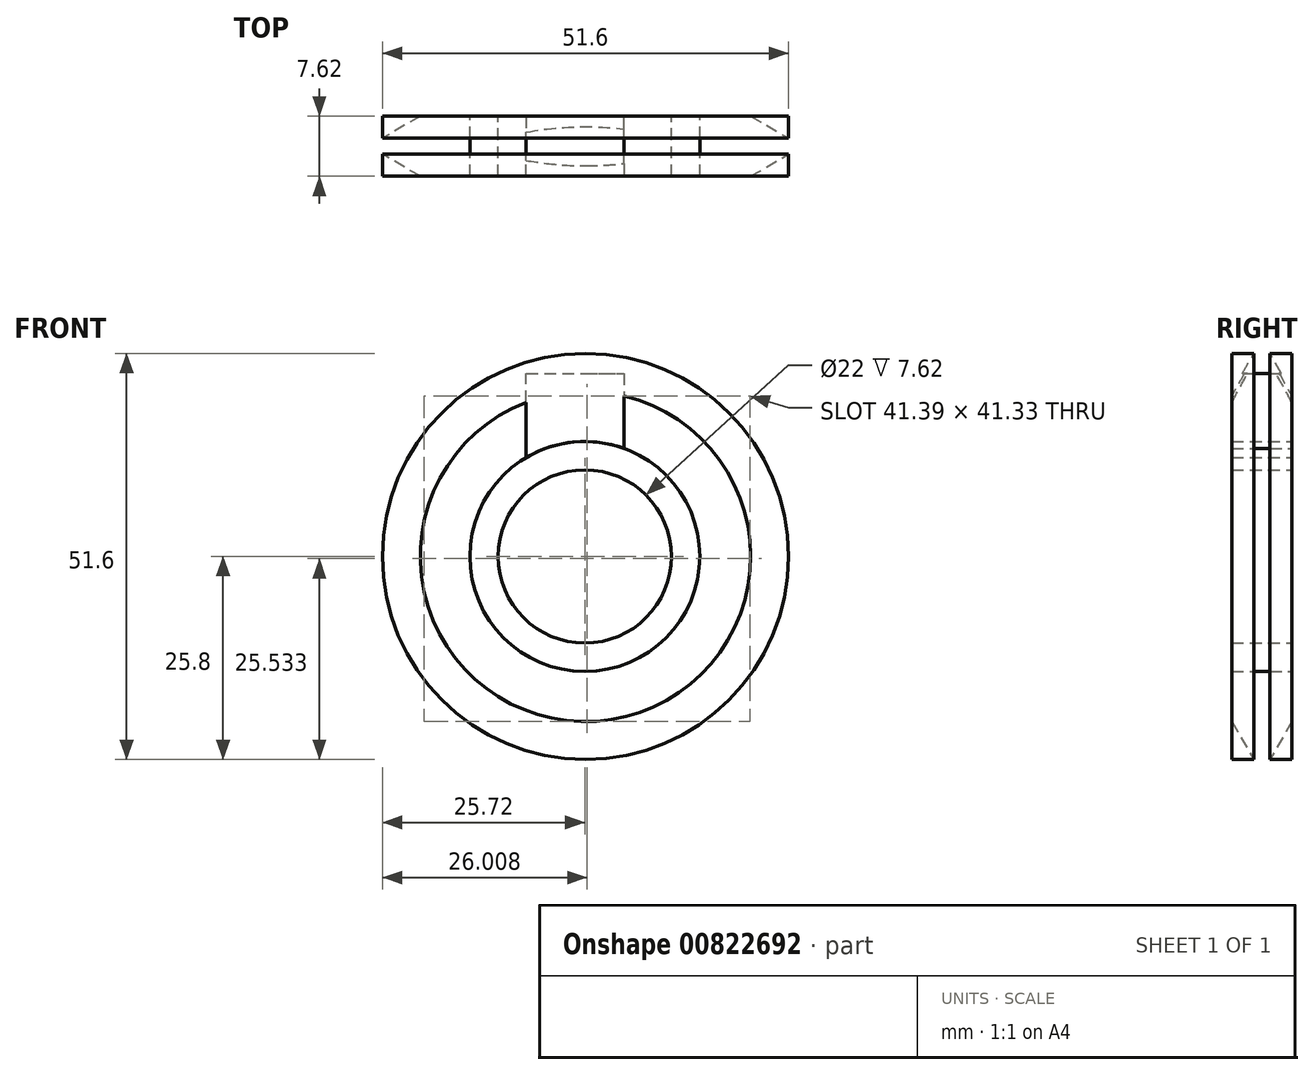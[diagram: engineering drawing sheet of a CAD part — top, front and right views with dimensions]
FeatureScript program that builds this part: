
annotation { "Feature Type Name" : "Feature", "Feature Type Description" : "" }
export const myFeature = defineFeature(function(context is Context, id is Id, definition is map)
    precondition{}
    {
        {
            var Q0;
            Q0=qCreatedBy(makeId("Front.planeOp"),FACE);
            var sketch = newSketch(context, id + "F0", { "sketchPlane" : qUnion([Q0])});
            skCircle(sketch, "E0", {"center": v(0, 0) * mm, "radius": 14.6 * mm});
            skCircle(sketch, "E1", {"center": v(0, 0) * mm, "radius": 11 * mm});
            skSolve(sketch);
        }
        {
            var Q0;
            Q0=qCreatedBy(makeId("Front.planeOp"),FACE);
            var sketch = newSketch(context, id + "F1", { "sketchPlane" : qUnion([Q0])});
            skLineSegment(sketch, "E2", {"start": v(-7.45, 12.56) * mm, "end": v(-7.45, 23.27) * mm});
            skLineSegment(sketch, "E3", {"start": v(-7.45, 23.27) * mm, "end": v(4.98, 23.27) * mm});
            skLineSegment(sketch, "E4", {"start": v(4.98, 23.27) * mm, "end": v(4.98, 13.62) * mm});
            skArc(sketch, "E5", {"start": v(-7.45, 12.56) * mm, "mid": v(-1.37, 14.54) * mm, "end": v(4.98, 13.73) * mm});
            skSolve(sketch);
        }
        {
            var Q0;
            Q0=makeQuery(id+"FBpl4X1R38b4iu1_0.1.F1.imprint","IMPRINT",FACE,{"disambiguationData":[TD([[makeQuery(id+"FBpl4X1R38b4iu1_0.1.F1.imprint","IMPRINT",EDGE,{"derivedFrom":sQuery(id+"FBpl4X1R38b4iu1_0.1.F1.wireOp",EDGE,"E2")}),-1.0]])]});
            var Q1;
            Q1=makeQuery(id+"FBpl4X1R38b4iu1_0.2.F1.imprint","IMPRINT",FACE,{"disambiguationData":[TD([[makeQuery(id+"FBpl4X1R38b4iu1_0.2.F1.imprint","IMPRINT",EDGE,{"derivedFrom":sQuery(id+"FBpl4X1R38b4iu1_0.2.F1.wireOp",EDGE,"E2")}),-1.0]])]});
            var Q2;
            Q2=makeQuery(id+"F1.imprint","IMPRINT",FACE,{"disambiguationData":[TD([[makeQuery(id+"F1.imprint","IMPRINT",EDGE,{"derivedFrom":sQuery(id+"F1.wireOp",EDGE,"E2")}),-1.0]])]});
            var Q3;
            Q3=makeQuery(id+"F0.imprint","IMPRINT",FACE,{"disambiguationData":[TD([[makeQuery(id+"F0.imprint","IMPRINT",EDGE,{"derivedFrom":sQuery(id+"F0.wireOp",EDGE,"E0")}),1.0]])]});
            extrude(context, id + "F2", {"entities" : qUnion([Q0, Q1, Q2, Q3]), "depth" : 7.62 * mm, "offsetDistance" : 25.4 * mm});
        }
        {
            var Q0;
            Q0=qCreatedBy(makeId("Top.planeOp"),FACE);
            var sketch = newSketch(context, id + "F3", { "sketchPlane" : qUnion([Q0])});
            skLineSegment(sketch, "E6", {"start": v(-20.9, 0) * mm, "end": v(-25.72, 0) * mm});
            skLineSegment(sketch, "E7", {"start": v(-25.72, 0) * mm, "end": v(-25.72, -2.79) * mm});
            skLineSegment(sketch, "E8", {"start": v(-25.72, -2.79) * mm, "end": v(-20.9, 0) * mm});
            skLineSegment(sketch, "E9", {"start": v(-12.87, -3.8) * mm, "end": v(-20.9, -3.81) * mm});
            skLineSegment(sketch, "E10.MirrorCS", {"start": v(-25.72, -7.62) * mm, "end": v(-25.72, -4.83) * mm});
            skLineSegment(sketch, "E11.MirrorCS", {"start": v(-25.72, -4.83) * mm, "end": v(-20.9, -7.62) * mm});
            skLineSegment(sketch, "E12.MirrorCS", {"start": v(-20.9, -7.62) * mm, "end": v(-25.72, -7.62) * mm});
            skLineSegment(sketch, "E13", {"start": v(0.08, 0.03) * mm, "end": v(0.08, -8.1) * mm});
            skSolve(sketch);
        }
        {
            var Q0;
            Q0=makeQuery(id+"F3.imprint","IMPRINT",FACE,{"disambiguationData":[TD([[makeQuery(id+"F3.imprint","IMPRINT",EDGE,{"derivedFrom":sQuery(id+"F3.wireOp",EDGE,"E6")}),1.0]])]});
            var Q1;
            Q1=makeQuery(id+"F3.imprint","IMPRINT",FACE,{"disambiguationData":[TD([[makeQuery(id+"F3.imprint","IMPRINT",EDGE,{"derivedFrom":sQuery(id+"F3.wireOp",EDGE,"E10.MirrorCS")}),-1.0]])]});
            var Q2;
            Q2=sQuery(id+"F3.wireOp",EDGE,"E13");
            revolve(context, id + "F4", {"operationType" : NewBodyOperationType.ADD, "surfaceOperationType" : NewSurfaceOperationType.NEW, "entities" : qUnion([Q0, Q1]), "axis" : qUnion([Q2]), "revolveType" : RevolveType.FULL});
        }
    });
